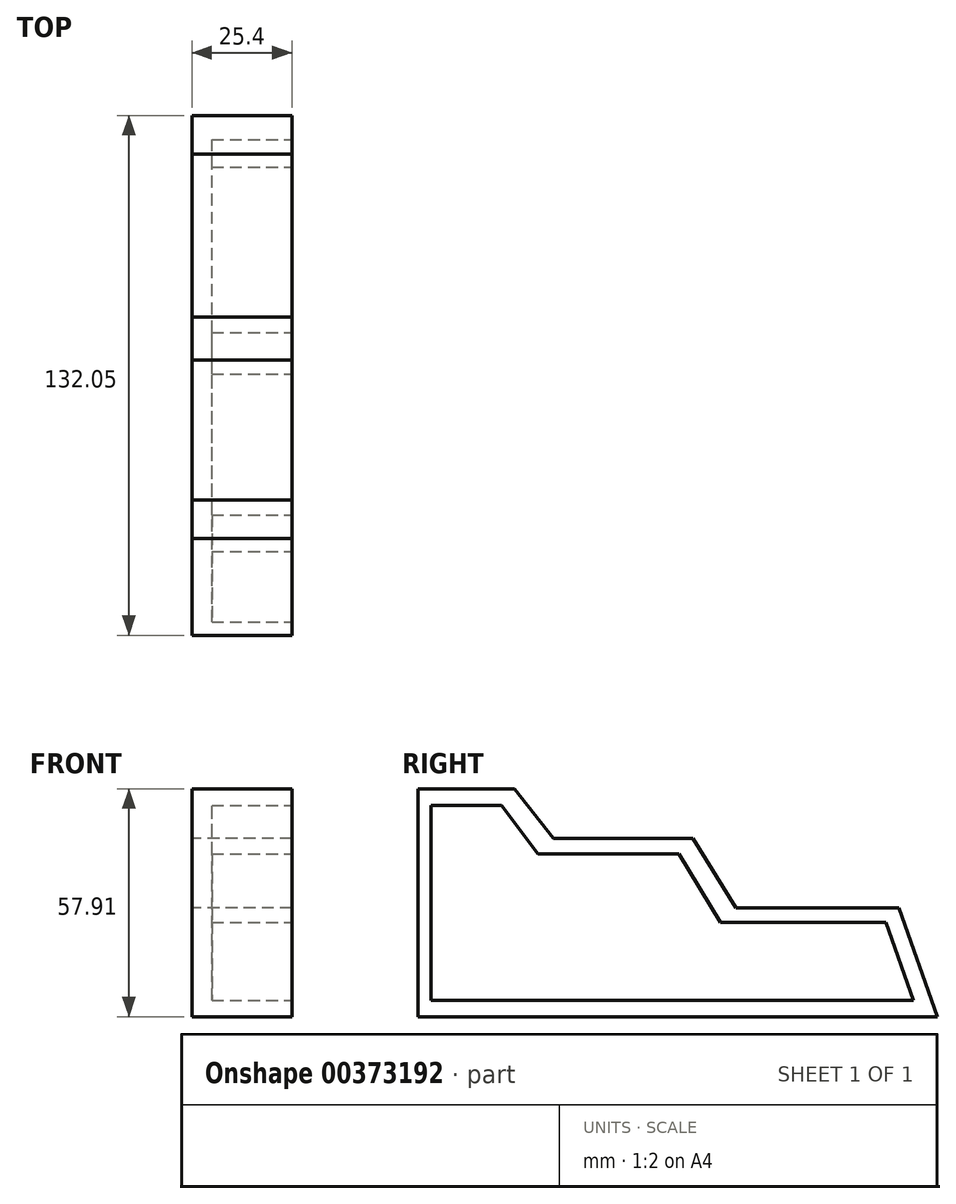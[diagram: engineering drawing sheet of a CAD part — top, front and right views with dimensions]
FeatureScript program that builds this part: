
annotation { "Feature Type Name" : "Feature", "Feature Type Description" : "" }
export const myFeature = defineFeature(function(context is Context, id is Id, definition is map)
    precondition{}
    {
        {
            var Q0;
            Q0=qCreatedBy(makeId("Right.planeOp"),FACE);
            var sketch = newSketch(context, id + "F0", { "sketchPlane" : qUnion([Q0])});
            skLineSegment(sketch, "E0", {"start": v(49.38, -8.67) * mm, "end": v(59.17, -36.37) * mm});
            skLineSegment(sketch, "E1", {"start": v(59.17, -36.37) * mm, "end": v(-72.88, -36.37) * mm});
            skLineSegment(sketch, "E2", {"start": v(-72.88, -36.37) * mm, "end": v(-72.88, -30.5) * mm});
            skLineSegment(sketch, "E3", {"start": v(49.38, -8.67) * mm, "end": v(7.97, -8.67) * mm});
            skLineSegment(sketch, "E4", {"start": v(7.97, -8.67) * mm, "end": v(-2.94, 8.95) * mm});
            skLineSegment(sketch, "E5", {"start": v(-2.94, 8.95) * mm, "end": v(-38.47, 8.95) * mm});
            skLineSegment(sketch, "E6", {"start": v(-38.47, 8.95) * mm, "end": v(-48.26, 21.54) * mm});
            skLineSegment(sketch, "E7", {"start": v(-48.26, 21.54) * mm, "end": v(-72.88, 21.54) * mm});
            skLineSegment(sketch, "E8", {"start": v(-72.88, 21.54) * mm, "end": v(-72.88, -30.5) * mm});
            skSolve(sketch);
        }
        {
            var Q0;
            Q0=makeQuery(id+"F0.imprint","IMPRINT",FACE,{"disambiguationData":[TD([[makeQuery(id+"F0.imprint","IMPRINT",EDGE,{"derivedFrom":sQuery(id+"F0.wireOp",EDGE,"E0")}),-1.0]])]});
            extrude(context, id + "F1", {"entities" : qUnion([Q0]), "depth" : 25.4 * mm});
        }
        {
            var Q0;
            Q0=qCreatedBy(makeId("Right.planeOp"),FACE);
            var sketch = newSketch(context, id + "F2", { "sketchPlane" : qUnion([Q0])});
            skLineSegment(sketch, "E9", {"start": v(-67.56, 17.34) * mm, "end": v(-67.56, -31.9) * mm});
            skLineSegment(sketch, "E10", {"start": v(-67.56, -31.9) * mm, "end": v(51.61, -31.9) * mm});
            skLineSegment(sketch, "E11", {"start": v(51.61, -31.9) * mm, "end": v(45.18, -13.43) * mm});
            skLineSegment(sketch, "E12", {"start": v(-6.3, 5.04) * mm, "end": v(-42.1, 5.04) * mm});
            skLineSegment(sketch, "E13", {"start": v(-42.1, 5.04) * mm, "end": v(-51.34, 17.62) * mm});
            skLineSegment(sketch, "E14", {"start": v(-67.56, 17.34) * mm, "end": v(-51.34, 17.62) * mm});
            skLineSegment(sketch, "E15", {"start": v(-6.3, 5.04) * mm, "end": v(5.46, -13.43) * mm});
            skLineSegment(sketch, "E16", {"start": v(5.46, -13.43) * mm, "end": v(45.18, -13.43) * mm});
            skSolve(sketch);
        }
        {
            var Q0;
            Q0 = qSketchRegion(id + "F2", true);
            extrude(context, id + "F3", {"entities" : qUnion([Q0]), "operationType" : NewBodyOperationType.REMOVE, "oppositeDirection" : true, "depth" : 25.4 * mm});
        }
        {
            var Q0;
            Q0=makeQuery(id+"F1.opExtrude","CAP_FACE",FACE,{"disambiguationData":[OSD([sQuery(id+"F0.wireOp",EDGE,"E0"),sQuery(id+"F0.wireOp",EDGE,"E1"),sQuery(id+"F0.wireOp",EDGE,"E2"),sQuery(id+"F0.wireOp",EDGE,"E3"),sQuery(id+"F0.wireOp",EDGE,"E4"),sQuery(id+"F0.wireOp",EDGE,"E5"),sQuery(id+"F0.wireOp",EDGE,"E6"),sQuery(id+"F0.wireOp",EDGE,"E7"),sQuery(id+"F0.wireOp",EDGE,"E8")])],"isStart":false});
            var sketch = newSketch(context, id + "F4", { "sketchPlane" : qUnion([Q0])});
            skLineSegment(sketch, "E17", {"start": v(-69.52, 17.34) * mm, "end": v(-69.52, -32.17) * mm});
            skLineSegment(sketch, "E18", {"start": v(-69.52, -32.17) * mm, "end": v(53.01, -32.17) * mm});
            skLineSegment(sketch, "E19", {"start": v(53.01, -32.17) * mm, "end": v(46.02, -12.4) * mm});
            skLineSegment(sketch, "E20", {"start": v(46.02, -12.4) * mm, "end": v(4.06, -12.4) * mm});
            skLineSegment(sketch, "E21", {"start": v(4.06, -12.4) * mm, "end": v(-6.57, 5.04) * mm});
            skLineSegment(sketch, "E22", {"start": v(-6.57, 5.04) * mm, "end": v(-42.38, 5.04) * mm});
            skLineSegment(sketch, "E23", {"start": v(-69.52, 17.34) * mm, "end": v(-51.61, 17.34) * mm});
            skLineSegment(sketch, "E24", {"start": v(-51.61, 17.34) * mm, "end": v(-42.38, 5.04) * mm});
            skSolve(sketch);
        }
        {
            var Q0;
            Q0=makeQuery(id+"F4.imprint","IMPRINT",FACE,{"disambiguationData":[TD([[makeQuery(id+"F4.imprint","IMPRINT",EDGE,{"derivedFrom":sQuery(id+"F4.wireOp",EDGE,"E17")}),1.0]])]});
            extrude(context, id + "F5", {"entities" : qUnion([Q0]), "operationType" : NewBodyOperationType.REMOVE, "oppositeDirection" : true, "depth" : 25.4 * mm});
        }
        {
            var Q0;
            Q0=qCreatedBy(makeId("Right.planeOp"),FACE);
            var sketch = newSketch(context, id + "F6", { "sketchPlane" : qUnion([Q0])});
            skLineSegment(sketch, "E25", {"start": v(45.74, -12.59) * mm, "end": v(53.01, -31.61) * mm});
            skLineSegment(sketch, "E26", {"start": v(53.01, -31.61) * mm, "end": v(-68.4, -31.61) * mm});
            skLineSegment(sketch, "E27", {"start": v(-51.34, 16.5) * mm, "end": v(-42.1, 4.2) * mm});
            skLineSegment(sketch, "E28", {"start": v(-42.1, 4.2) * mm, "end": v(-6.01, 4.2) * mm});
            skLineSegment(sketch, "E29", {"start": v(-6.01, 4.2) * mm, "end": v(4.34, -12.87) * mm});
            skLineSegment(sketch, "E30", {"start": v(4.34, -12.87) * mm, "end": v(45.74, -12.59) * mm});
            skLineSegment(sketch, "E31", {"start": v(-68.96, 16.5) * mm, "end": v(-68.4, -31.61) * mm});
            skLineSegment(sketch, "E32", {"start": v(-51.34, 16.5) * mm, "end": v(-68.96, 16.5) * mm});
            skSolve(sketch);
        }
        {
            var Q0;
            Q0=makeQuery(id+"F6.imprint","IMPRINT",FACE,{"disambiguationData":[TD([[makeQuery(id+"F6.imprint","IMPRINT",EDGE,{"derivedFrom":sQuery(id+"F6.wireOp",EDGE,"E25")}),-1.0]])]});
            extrude(context, id + "F7", {"entities" : qUnion([Q0]), "operationType" : NewBodyOperationType.ADD, "depth" : 5.08 * mm});
        }
        {
            var Q0;
            Q0=qCreatedBy(makeId("Right.planeOp"),FACE);
            var sketch = newSketch(context, id + "F8", { "sketchPlane" : qUnion([Q0])});
            skLineSegment(sketch, "E33", {"start": v(-7.41, 4.76) * mm, "end": v(-42.1, 4.76) * mm});
            skLineSegment(sketch, "E34", {"start": v(-42.1, 4.76) * mm, "end": v(-50.78, 17.07) * mm});
            skLineSegment(sketch, "E35", {"start": v(-50.78, 17.07) * mm, "end": v(-69.8, 17.07) * mm});
            skLineSegment(sketch, "E36", {"start": v(-69.8, 17.07) * mm, "end": v(-69.8, -30.21) * mm});
            skLineSegment(sketch, "E37", {"start": v(-69.8, -32.17) * mm, "end": v(53.01, -32.17) * mm});
            skLineSegment(sketch, "E38", {"start": v(53.01, -32.17) * mm, "end": v(46.86, -11.75) * mm});
            skLineSegment(sketch, "E39", {"start": v(46.86, -11.75) * mm, "end": v(5.46, -11.75) * mm});
            skLineSegment(sketch, "E40", {"start": v(5.46, -11.75) * mm, "end": v(-7.41, 4.76) * mm});
            skLineSegment(sketch, "E41", {"start": v(-69.8, -32.17) * mm, "end": v(-69.8, -30.21) * mm});
            skSolve(sketch);
        }
        {
            var Q0;
            Q0=qCreatedBy(makeId("Right.planeOp"),FACE);
            var sketch = newSketch(context, id + "F9", { "sketchPlane" : qUnion([Q0])});
            skLineSegment(sketch, "E42", {"start": v(49.11, -13.1) * mm, "end": v(56.29, -33.45) * mm});
            skLineSegment(sketch, "E43", {"start": v(56.29, -33.45) * mm, "end": v(-70.44, -33.45) * mm});
            skLineSegment(sketch, "E44", {"start": v(-70.44, -33.45) * mm, "end": v(-70.44, 18.85) * mm});
            skLineSegment(sketch, "E45", {"start": v(-70.44, 18.85) * mm, "end": v(-49.65, 18.85) * mm});
            skLineSegment(sketch, "E46", {"start": v(-49.65, 18.85) * mm, "end": v(-40.6, 6.53) * mm});
            skLineSegment(sketch, "E47", {"start": v(-40.6, 6.53) * mm, "end": v(-4.5, 6.53) * mm});
            skLineSegment(sketch, "E48", {"start": v(-4.5, 6.53) * mm, "end": v(7.4, -10.67) * mm});
            skLineSegment(sketch, "E49", {"start": v(7.4, -10.67) * mm, "end": v(49.11, -10.67) * mm});
            skLineSegment(sketch, "E50", {"start": v(49.11, -10.67) * mm, "end": v(49.11, -13.1) * mm});
            skSolve(sketch);
        }
        {
            var Q0;
            Q0=makeQuery(id+"F8.imprint","IMPRINT",FACE,{"disambiguationData":[TD([[makeQuery(id+"F8.imprint","IMPRINT",EDGE,{"derivedFrom":sQuery(id+"F8.wireOp",EDGE,"E33")}),1.0]])]});
            extrude(context, id + "F10", {"entities" : qUnion([Q0]), "operationType" : NewBodyOperationType.ADD, "depth" : 5.08 * mm});
        }
        {
            var Q0;
            Q0=makeQuery(id+"F9.imprint","IMPRINT",FACE,{"disambiguationData":[TD([[makeQuery(id+"F9.imprint","IMPRINT",EDGE,{"derivedFrom":sQuery(id+"F9.wireOp",EDGE,"E42")}),-1.0]])]});
            extrude(context, id + "F11", {"entities" : qUnion([Q0]), "operationType" : NewBodyOperationType.ADD, "depth" : 5.08 * mm});
        }
    });
